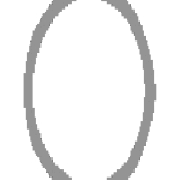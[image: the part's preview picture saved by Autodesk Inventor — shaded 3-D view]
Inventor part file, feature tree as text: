
AUTODESK INVENTOR PART (.ipt)
format: ipt  version: 2021 (Build 250183000, 183)  size: 112,128 bytes
history: native  units: in
note: dims shown in document units (in); Inventor stores cm internally (conversion verified against a paired STEP export)
features: other x4, sketch x3, plane x1
ambient origin geometry x8: Origin, YZ Plane, XZ Plane, XY Plane, X Axis, Y Axis, Z Axis, Center Point
bodies: Solid1 (feature_tree), Body (feature_tree)
feature tree (8):
  other  "Driven Length"
  other  "Frame Generator"
  other  "Start Plane"
  other  "End Plane"
  sketch  "Sketch"  dims[d2=20.5in d4=-0.0in d5=20.5in d6=0.12in d7=0.0in d8=90.0deg d9=20.5in]
  sketch  "Sketch2"  dims[d0=1.0in]
  plane  "Work Plane3"
  sketch  "Sketch3"  dims[d1=0.065in]
